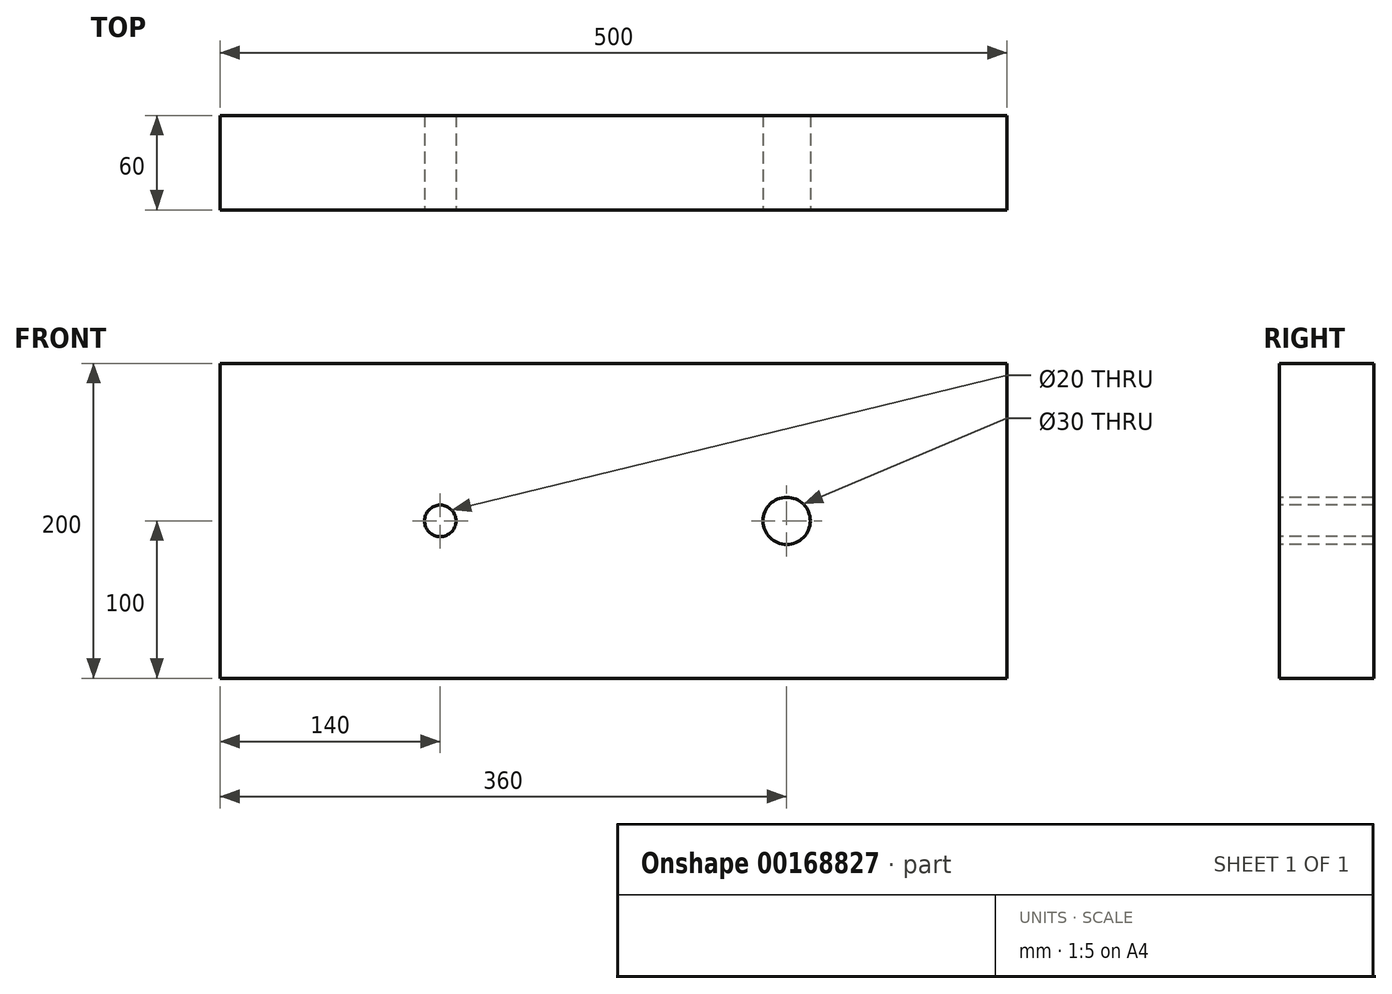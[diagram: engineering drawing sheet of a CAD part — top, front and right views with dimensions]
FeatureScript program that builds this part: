
annotation { "Feature Type Name" : "Feature", "Feature Type Description" : "" }
export const myFeature = defineFeature(function(context is Context, id is Id, definition is map)
    precondition{}
    {
        {
            assignVariable(context, id + "F0", {"name" : "t", "anyValue" : 60 * mm});
        }
        {
            var Q0;
            Q0=qCreatedBy(makeId("Front.planeOp"),FACE);
            var sketch = newSketch(context, id + "F1", { "sketchPlane" : qUnion([Q0])});
            skLineSegment(sketch, "E0.bottom", {"start": v(250, -100) * mm, "end": v(-250, -100) * mm});
            skLineSegment(sketch, "E0.top", {"start": v(250, 100) * mm, "end": v(-250, 100) * mm});
            skLineSegment(sketch, "E0.left", {"start": v(250, -100) * mm, "end": v(250, 100) * mm});
            skLineSegment(sketch, "E0.right", {"start": v(-250, -100) * mm, "end": v(-250, 100) * mm});
            skPoint(sketch, "E0.middle", {"position": v(0, 0) * mm});
            skSolve(sketch);
        }
        {
            var Q0;
            Q0 = qSketchRegion(id + "F1", true);
            extrude(context, id + "F2", {"entities" : qUnion([Q0]), "depth" : getVariable(context, 't')});
        }
        {
            var Q0;
            Q0=makeQuery(id+"F2.opExtrude","CAP_FACE",FACE,{"disambiguationData":[OSD([sQuery(id+"F1.wireOp",EDGE,"E0.bottom"),sQuery(id+"F1.wireOp",EDGE,"E0.top"),sQuery(id+"F1.wireOp",EDGE,"E0.left"),sQuery(id+"F1.wireOp",EDGE,"E0.right")])],"isStart":false});
            var sketch = newSketch(context, id + "F3", { "sketchPlane" : qUnion([Q0])});
            skCircle(sketch, "E1", {"center": v(110, 0) * mm, "radius": 15 * mm});
            skLineSegment(sketch, "E2", {"start": v(110, 100) * mm, "end": v(110, 0) * mm, "construction": true});
            skLineSegment(sketch, "E3", {"start": v(250, 0) * mm, "end": v(110, 0) * mm, "construction": true});
            skCircle(sketch, "E4", {"center": v(-110, 0) * mm, "radius": 10 * mm});
            skLineSegment(sketch, "E5", {"start": v(-110, 0) * mm, "end": v(-110, 100) * mm, "construction": true});
            skLineSegment(sketch, "E6", {"start": v(-110, 0) * mm, "end": v(-250, 0) * mm, "construction": true});
            skSolve(sketch);
        }
        {
            var Q0;
            Q0 = qSketchRegion(id + "F3", true);
            extrude(context, id + "F4", {"entities" : qUnion([Q0]), "operationType" : NewBodyOperationType.REMOVE, "endBound" : BoundingType.THROUGH_ALL, "oppositeDirection" : true, "depth" : 25 * mm});
        }
    });
